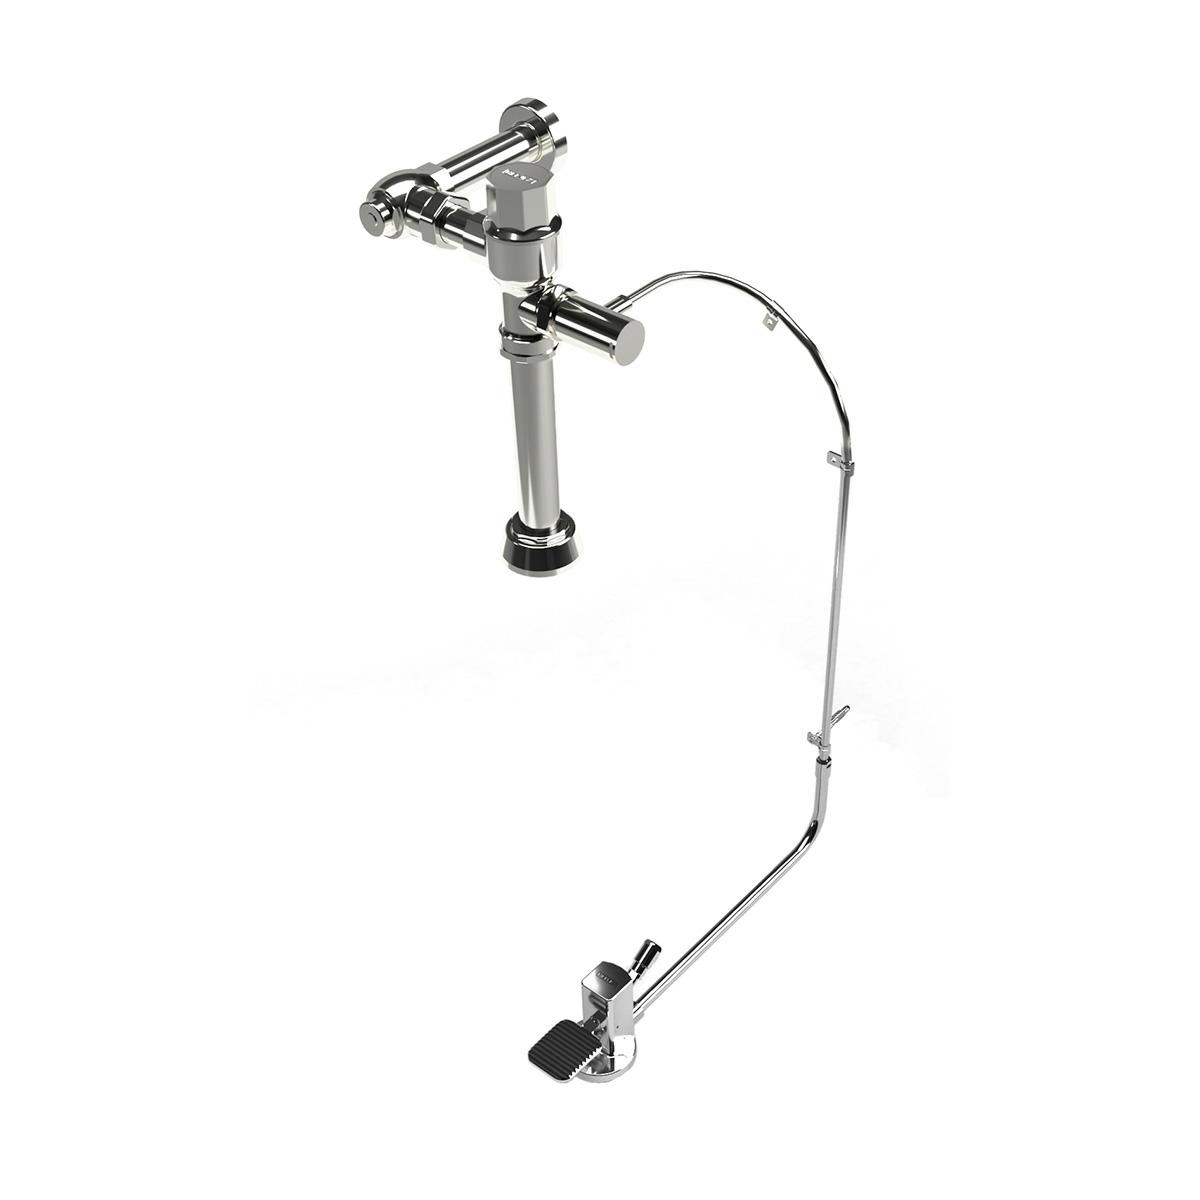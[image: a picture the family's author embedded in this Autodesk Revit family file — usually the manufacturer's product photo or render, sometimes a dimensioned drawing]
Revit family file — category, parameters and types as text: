
# Revit family: 313-38-3.5
name_source: partatom
category: Aparatos sanitarios
units: mm (PartAtom-declared; Revit-internal decimal feet)

## family parameters
Compartido = Sí
Corte con vacíos al cargar = No
Cota de conector redondo = Diámetro de uso
Número OmniClass = 23.45.00.00
Punto de cálculo de habitación = No
Se basa en plano de trabajo = No
Siempre vertical = Sí
Tipo de pieza = Normal
Título OmniClass = Sanitary, Laundry, and Cleaning Equipment

## types (1)
- 313-38-4.8
    Chrome = Brass Chromed
    Comentarios de tipo = Fluxómetro de pedal expuesto 3.5 LPD
    Conexión AF = Sí
    Connection = Conexión de alimentación: tubo 25,4 mm
    Descripción = Fluxómetro de pedal expuesto 3.5 LPD
    Documentation = https://www.helvex.com.mx
    Elevación por defecto = 0"
    Fabricante = HELVEX
    Imagen de tipo = 313-38-3.5.jpg
    Instructive = https://www.helvex.com.mx
    Max. Working Pressure = 85.3 psi
    Min. Working Pressure = 28.4 psi
    Modelo = 313-38-3.5
    Note = Conexión de descarga: Spud 38 mm
    URL = https://www.helvex.com.mx

## geometry (parser evidence)
native form markers: Sweep x3
no freeform markers — native parametric forms only
